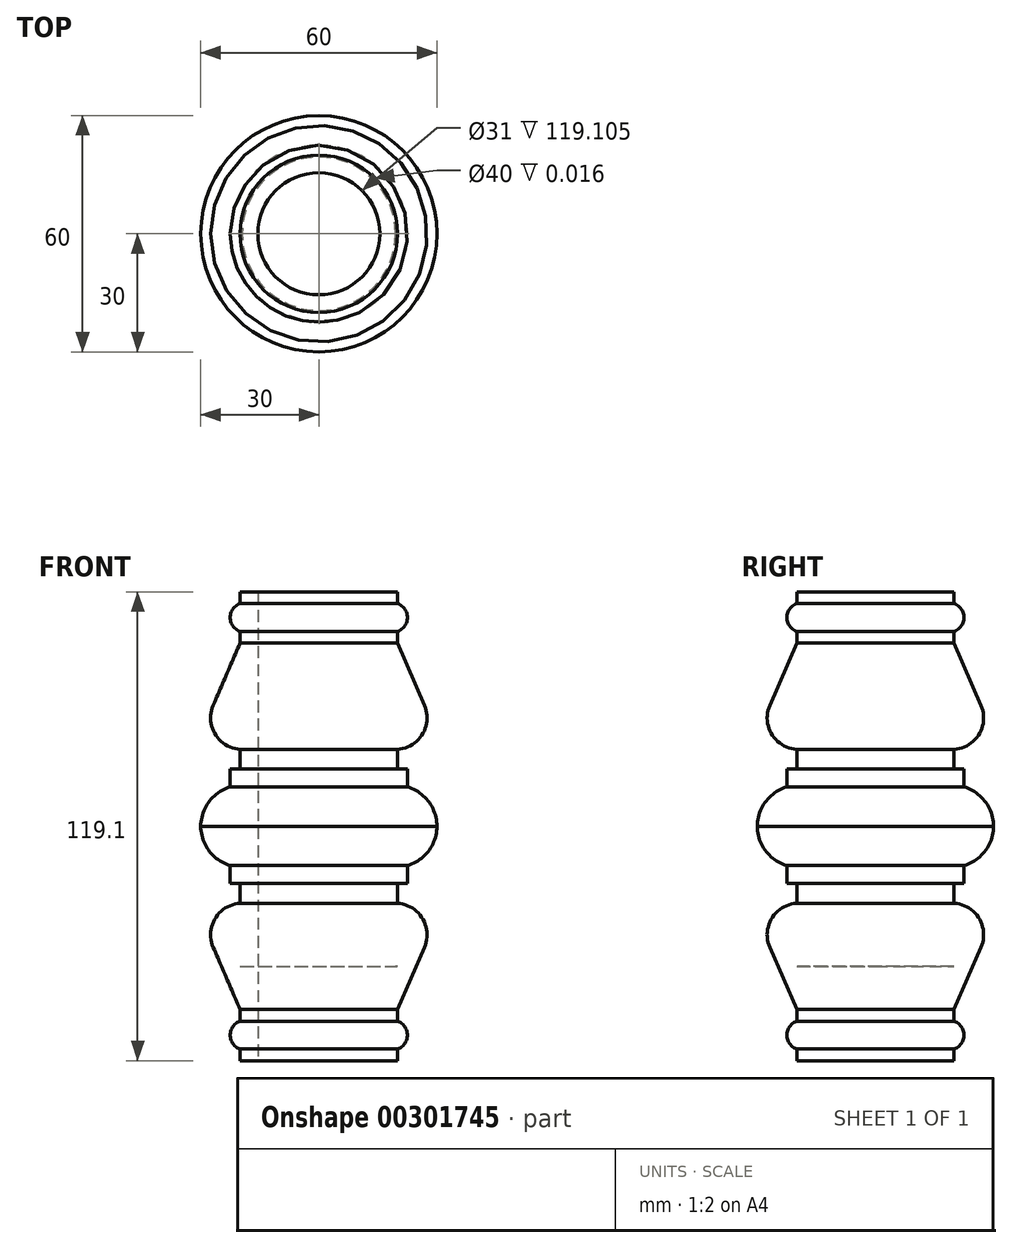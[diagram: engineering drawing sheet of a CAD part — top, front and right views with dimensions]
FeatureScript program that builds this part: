
annotation { "Feature Type Name" : "Feature", "Feature Type Description" : "" }
export const myFeature = defineFeature(function(context is Context, id is Id, definition is map)
    precondition{}
    {
        {
            var Q0;
            Q0=qCreatedBy(makeId("Front.planeOp"),FACE);
            var sketch = newSketch(context, id + "F0", { "sketchPlane" : qUnion([Q0])});
            skLineSegment(sketch, "E0.bottom", {"start": v(-20, 0) * mm, "end": v(-40, 0) * mm});
            skLineSegment(sketch, "E0.right", {"start": v(-40, 0) * mm, "end": v(-40, 3) * mm});
            skLineSegment(sketch, "E1", {"start": v(-37.5, 10) * mm, "end": v(-40, 10) * mm});
            skPoint(sketch, "E2.start.orphan", {"position": v(-42.5, 2.94) * mm});
            skLineSegment(sketch, "E3", {"start": v(-40, 10) * mm, "end": v(-40, 13) * mm});
            skLineSegment(sketch, "E4", {"start": v(-40, 24) * mm, "end": v(-40, 24.02) * mm});
            skPoint(sketch, "E5.centerSnap0", {"position": v(-42, 32) * mm});
            skLineSegment(sketch, "E6", {"start": v(-40, 3) * mm, "end": v(-37.5, 3) * mm});
            skLineSegment(sketch, "E7", {"start": v(-40.1, 10) * mm, "end": v(-40, 10) * mm});
            skArc(sketch, "E8", {"start": v(-40, 10.04) * mm, "mid": v(-42.5, 6.5) * mm, "end": v(-40, 2.96) * mm});
            skPoint(sketch, "E8.centerSnap0", {"position": v(-37.5, 6.5) * mm});
            skPoint(sketch, "E8.centerSnap1", {"position": v(-38.75, 3) * mm});
            skPoint(sketch, "E9.orphan", {"position": v(-37.5, 10) * mm});
            skLineSegment(sketch, "E10.trimOffspring", {"start": v(-42, 24.25) * mm, "end": v(-42, 24) * mm, "construction": true});
            skPoint(sketch, "E5.center.orphan", {"position": v(-40, 32) * mm});
            skPoint(sketch, "E11.start.orphan", {"position": v(-42, 40) * mm});
            skLineSegment(sketch, "E12", {"start": v(-40, 32) * mm, "end": v(-39.5, 32) * mm});
            skLineSegment(sketch, "E13", {"start": v(-40, 40) * mm, "end": v(-40, 39.98) * mm});
            skLineSegment(sketch, "E14", {"start": v(-40, 24) * mm, "end": v(-39.5, 24) * mm});
            skPoint(sketch, "E15.endSnap0", {"position": v(-38.13, 32) * mm});
            skArc(sketch, "E16", {"start": v(-40, 24.02) * mm, "mid": v(-39.75, 24) * mm, "end": v(-39.5, 24) * mm});
            skArc(sketch, "E17.trimOffspring", {"start": v(-39.5, 40) * mm, "mid": v(-46.19, 36.4) * mm, "end": v(-46.84, 28.82) * mm});
            skPoint(sketch, "E18.orphan", {"position": v(-36.25, 32) * mm});
            skLineSegment(sketch, "E19.trimOffspring", {"start": v(-40, 24.02) * mm, "end": v(-40, 24) * mm});
            skLineSegment(sketch, "E20.trimOffspring", {"start": v(-40, 39.98) * mm, "end": v(-40, 40) * mm});
            skLineSegment(sketch, "E21", {"start": v(-40, 40) * mm, "end": v(-40, 45) * mm});
            skLineSegment(sketch, "E22", {"start": v(-40, 45) * mm, "end": v(-20, 45) * mm});
            skLineSegment(sketch, "E23", {"start": v(-40, 45) * mm, "end": v(-42.5, 45) * mm});
            skLineSegment(sketch, "E24", {"start": v(-42.5, 45) * mm, "end": v(-42.5, 49.55) * mm});
            skLineSegment(sketch, "E25", {"start": v(-42.5, 49.55) * mm, "end": v(-20, 49.55) * mm});
            skLineSegment(sketch, "E26", {"start": v(-42.5, 69.55) * mm, "end": v(-20, 69.55) * mm});
            skLineSegment(sketch, "E27", {"start": v(-40, 13) * mm, "end": v(-46.84, 28.82) * mm});
            skPoint(sketch, "E28.endSnap0", {"position": v(-50, 59.55) * mm});
            skArc(sketch, "E29", {"start": v(-50, 59.55) * mm, "mid": v(-47.9, 53.31) * mm, "end": v(-42.5, 49.55) * mm});
            skArc(sketch, "E30.MirrorCS", {"start": v(-50, 59.55) * mm, "mid": v(-47.9, 65.79) * mm, "end": v(-42.5, 69.55) * mm});
            skPoint(sketch, "E28.end.orphan", {"position": v(-38.75, 59.55) * mm});
            skPoint(sketch, "E31.start.orphan", {"position": v(-42.5, 69.55) * mm});
            skPoint(sketch, "E32.orphan", {"position": v(-50, 69.55) * mm});
            skPoint(sketch, "E33.end.orphan", {"position": v(-50, 49.55) * mm});
            skLineSegment(sketch, "E34.MirrorCS", {"start": v(-40, 79.1) * mm, "end": v(-40, 79.12) * mm});
            skLineSegment(sketch, "E35.MirrorCS", {"start": v(-40, 79.12) * mm, "end": v(-40, 79.1) * mm});
            skLineSegment(sketch, "E36.MirrorCS", {"start": v(-40, 87.1) * mm, "end": v(-39.5, 87.1) * mm});
            skLineSegment(sketch, "E37.MirrorCS", {"start": v(-40, 79.1) * mm, "end": v(-40, 74.1) * mm});
            skLineSegment(sketch, "E38.MirrorCS", {"start": v(-40, 74.1) * mm, "end": v(-42.5, 74.1) * mm});
            skLineSegment(sketch, "E39.MirrorCS", {"start": v(-40.1, 109.1) * mm, "end": v(-40, 109.1) * mm});
            skLineSegment(sketch, "E40.MirrorCS", {"start": v(-40, 119.1) * mm, "end": v(-40, 116.1) * mm});
            skLineSegment(sketch, "E41.MirrorCS", {"start": v(-40, 116.1) * mm, "end": v(-37.5, 116.1) * mm});
            skArc(sketch, "E42.MirrorCS", {"start": v(-40, 109.07) * mm, "mid": v(-42.5, 112.6) * mm, "end": v(-40, 116.14) * mm});
            skLineSegment(sketch, "E43.MirrorCS", {"start": v(-40, 109.1) * mm, "end": v(-40, 106.1) * mm});
            skLineSegment(sketch, "E44.MirrorCS", {"start": v(-42, 94.85) * mm, "end": v(-42, 95.1) * mm, "construction": true});
            skArc(sketch, "E45.MirrorCS", {"start": v(-40, 95.09) * mm, "mid": v(-39.75, 95.1) * mm, "end": v(-39.5, 95.1) * mm});
            skLineSegment(sketch, "E46.MirrorCS", {"start": v(-42.5, 74.1) * mm, "end": v(-42.5, 69.55) * mm});
            skLineSegment(sketch, "E47.MirrorCS", {"start": v(-40, 106.1) * mm, "end": v(-46.84, 90.28) * mm});
            skArc(sketch, "E48.MirrorCS", {"start": v(-39.5, 79.1) * mm, "mid": v(-46.19, 82.71) * mm, "end": v(-46.84, 90.28) * mm});
            skPoint(sketch, "E49.MirrorP", {"position": v(-38.13, 87.1) * mm});
            skPoint(sketch, "E50.MirrorP", {"position": v(-42, 87.1) * mm});
            skPoint(sketch, "E51.MirrorP", {"position": v(-36.25, 87.1) * mm});
            skPoint(sketch, "E52.MirrorP", {"position": v(-38.75, 116.1) * mm});
            skPoint(sketch, "E53.MirrorP", {"position": v(-37.5, 112.6) * mm});
            skLineSegment(sketch, "E54.MirrorCS", {"start": v(-40, 74.1) * mm, "end": v(-20, 74.1) * mm});
            skLineSegment(sketch, "E55.MirrorCS", {"start": v(-20, 119.1) * mm, "end": v(-40, 119.1) * mm});
            skLineSegment(sketch, "E56.MirrorCS", {"start": v(-40, 79.1) * mm, "end": v(-39.5, 79.1) * mm});
            skPoint(sketch, "E57.MirrorP", {"position": v(-37.5, 109.1) * mm});
            skLineSegment(sketch, "E58.MirrorCS", {"start": v(-37.5, 109.1) * mm, "end": v(-40, 109.1) * mm});
            skPoint(sketch, "E59.MirrorP", {"position": v(-42.5, 116.17) * mm});
            skPoint(sketch, "E60.MirrorP", {"position": v(-42, 79.1) * mm});
            skLineSegment(sketch, "E61.MirrorCS", {"start": v(-40, 95.1) * mm, "end": v(-39.5, 95.1) * mm});
            skPoint(sketch, "E62.MirrorP", {"position": v(-40, 87.1) * mm});
            skLineSegment(sketch, "E63.MirrorCS", {"start": v(-40, 106.1) * mm, "end": v(-20, 106.1) * mm});
            skPoint(sketch, "E64.orphan", {"position": v(-42.5, 109.17) * mm});
            skPoint(sketch, "E65.orphan", {"position": v(-47.5, 87.1) * mm});
            skPoint(sketch, "E66.orphan", {"position": v(-47.5, 78.18) * mm});
            skPoint(sketch, "E67.MirrorCS.end.orphan", {"position": v(-47.5, 106.1) * mm});
            skPoint(sketch, "E68.end.orphan", {"position": v(-47.5, 13) * mm});
            skPoint(sketch, "E69.orphan", {"position": v(-47.5, 32) * mm});
            skLineSegment(sketch, "E70", {"start": v(-20, 0) * mm, "end": v(-20, 119.1) * mm});
            skLineSegment(sketch, "E71", {"start": v(-20, 116.1) * mm, "end": v(-20, 119.1) * mm});
            skLineSegment(sketch, "E72", {"start": v(-20, 109.1) * mm, "end": v(-20, 116.1) * mm});
            skLineSegment(sketch, "E73", {"start": v(-20, 106.1) * mm, "end": v(-20, 109.1) * mm});
            skLineSegment(sketch, "E74", {"start": v(-20, 79.1) * mm, "end": v(-20, 106.1) * mm});
            skLineSegment(sketch, "E75", {"start": v(-20, 74.1) * mm, "end": v(-20, 79.1) * mm});
            skLineSegment(sketch, "E76", {"start": v(-20, 69.55) * mm, "end": v(-20, 74.1) * mm});
            skLineSegment(sketch, "E77", {"start": v(-20, 49.55) * mm, "end": v(-20, 69.55) * mm});
            skLineSegment(sketch, "E78", {"start": v(-20, 45) * mm, "end": v(-20, 49.55) * mm});
            skLineSegment(sketch, "E79", {"start": v(-20, 40) * mm, "end": v(-20, 45) * mm});
            skLineSegment(sketch, "E80", {"start": v(-20, 13) * mm, "end": v(-20, 40) * mm});
            skLineSegment(sketch, "E81", {"start": v(-20, 10) * mm, "end": v(-20, 13) * mm});
            skLineSegment(sketch, "E82", {"start": v(-20, 3) * mm, "end": v(-20, 10) * mm});
            skLineSegment(sketch, "E83", {"start": v(-20, 0) * mm, "end": v(-20, 3) * mm});
            skLineSegment(sketch, "E84", {"start": v(-20, 3) * mm, "end": v(-37.5, 3) * mm});
            skLineSegment(sketch, "E85", {"start": v(-20, 10) * mm, "end": v(-40, 10.04) * mm});
            skLineSegment(sketch, "E86", {"start": v(-20, 13) * mm, "end": v(-40, 13) * mm});
            skLineSegment(sketch, "E87", {"start": v(-20, 40) * mm, "end": v(-40, 40) * mm});
            skLineSegment(sketch, "E88", {"start": v(-20, 45) * mm, "end": v(-40, 45) * mm});
            skLineSegment(sketch, "E89", {"start": v(-20, 49.55) * mm, "end": v(-42.5, 49.55) * mm});
            skLineSegment(sketch, "E90", {"start": v(-20, 69.55) * mm, "end": v(-42.5, 69.55) * mm});
            skLineSegment(sketch, "E91", {"start": v(-20, 74.1) * mm, "end": v(-42.5, 74.1) * mm});
            skLineSegment(sketch, "E92", {"start": v(-20, 79.1) * mm, "end": v(-39.5, 79.1) * mm});
            skLineSegment(sketch, "E93", {"start": v(-20, 106.1) * mm, "end": v(-40, 106.1) * mm});
            skLineSegment(sketch, "E94", {"start": v(-20, 109.1) * mm, "end": v(-40, 109.1) * mm});
            skLineSegment(sketch, "E95", {"start": v(-20, 116.1) * mm, "end": v(-38.75, 116.1) * mm});
            skLineSegment(sketch, "E96.trimOffspring", {"start": v(-20, 3) * mm, "end": v(-40, 3) * mm});
            skLineSegment(sketch, "E97.trimOffspring", {"start": v(-20, 116.1) * mm, "end": v(-40, 116.1) * mm});
            skSolve(sketch);
        }
        {
            var Q0;
            Q0 = qSketchRegion(id + "F0", true);
            var Q1;
            Q1=sQuery(id+"F0.wireOp",EDGE,"E70");
            revolve(context, id + "F1", {"entities" : qUnion([Q0]), "axis" : qUnion([Q1]), "revolveType" : RevolveType.FULL});
        }
        {
            var Q0;
            Q0=qCreatedBy(makeId("Top.planeOp"),FACE);
            var sketch = newSketch(context, id + "F2", { "sketchPlane" : qUnion([Q0])});
            skLineSegment(sketch, "E98", {"start": v(0, 0) * mm, "end": v(-40, 0) * mm});
            skCircle(sketch, "E99", {"center": v(-20, 0) * mm, "radius": 15.5 * mm});
            skSolve(sketch);
        }
        {
            var Q0;
            {var subQ0=sQuery(id+"F2.wireOp",EDGE,"E99");var subQ1=sQuery(id+"F2.wireOp",EDGE,"E98");var subQ2=makeQuery(id+"F2.imprint","INTERSECT",VERTEX,{"disambiguationData":[OD(0.0)],"derivedFrom":[subQ1,subQ0]});Q0=makeQuery(id+"F2.imprint","IMPRINT",FACE,{"disambiguationData":[TD([[makeQuery(id+"F2.imprint","IMPRINT",EDGE,{"disambiguationData":[TD([[subQ2,1.0]])],"derivedFrom":subQ1}),1.0]])]});}
            var Q1;
            {var subQ0=sQuery(id+"F2.wireOp",EDGE,"E99");var subQ1=sQuery(id+"F2.wireOp",EDGE,"E98");var subQ2=makeQuery(id+"F2.imprint","INTERSECT",VERTEX,{"disambiguationData":[OD(0.0)],"derivedFrom":[subQ1,subQ0]});Q1=makeQuery(id+"F2.imprint","IMPRINT",FACE,{"disambiguationData":[TD([[makeQuery(id+"F2.imprint","IMPRINT",EDGE,{"disambiguationData":[TD([[subQ2,1.0]])],"derivedFrom":subQ1}),-1.0]])]});}
            extrude(context, id + "F3", {"entities" : qUnion([Q0, Q1]), "operationType" : NewBodyOperationType.REMOVE, "depth" : 120 * mm});
        }
    });
